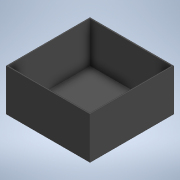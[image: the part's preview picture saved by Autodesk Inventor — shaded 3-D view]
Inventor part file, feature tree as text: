
AUTODESK INVENTOR PART (.ipt)
format: ipt  version: 2020 (Build 240168000, 168)  size: 117,760 bytes
history: native  units: mm
features: extrude x2, sketch x2, other x1
ambient origin geometry x8: Origin, YZ Plane, XZ Plane, XY Plane, X Axis, Y Axis, Z Axis, Center Point
bodies: Body1 (feature_tree)
feature tree (5):
  other  "Sólido1"
  extrude  "Extrusión1"  Depth=200.0mm
  extrude  "Extrusión2"  Depth=390.0mm
  sketch  "Boceto1"  dims[d1=400.0mm d2=200.0mm]
  sketch  "Boceto2"  dims[d3=200.0mm d4=390.0mm d5=390.0mm d6=195.0mm d7=195.0mm d8=200.0mm d9=0.0mm d10=5.0mm d11=0.0mm]
